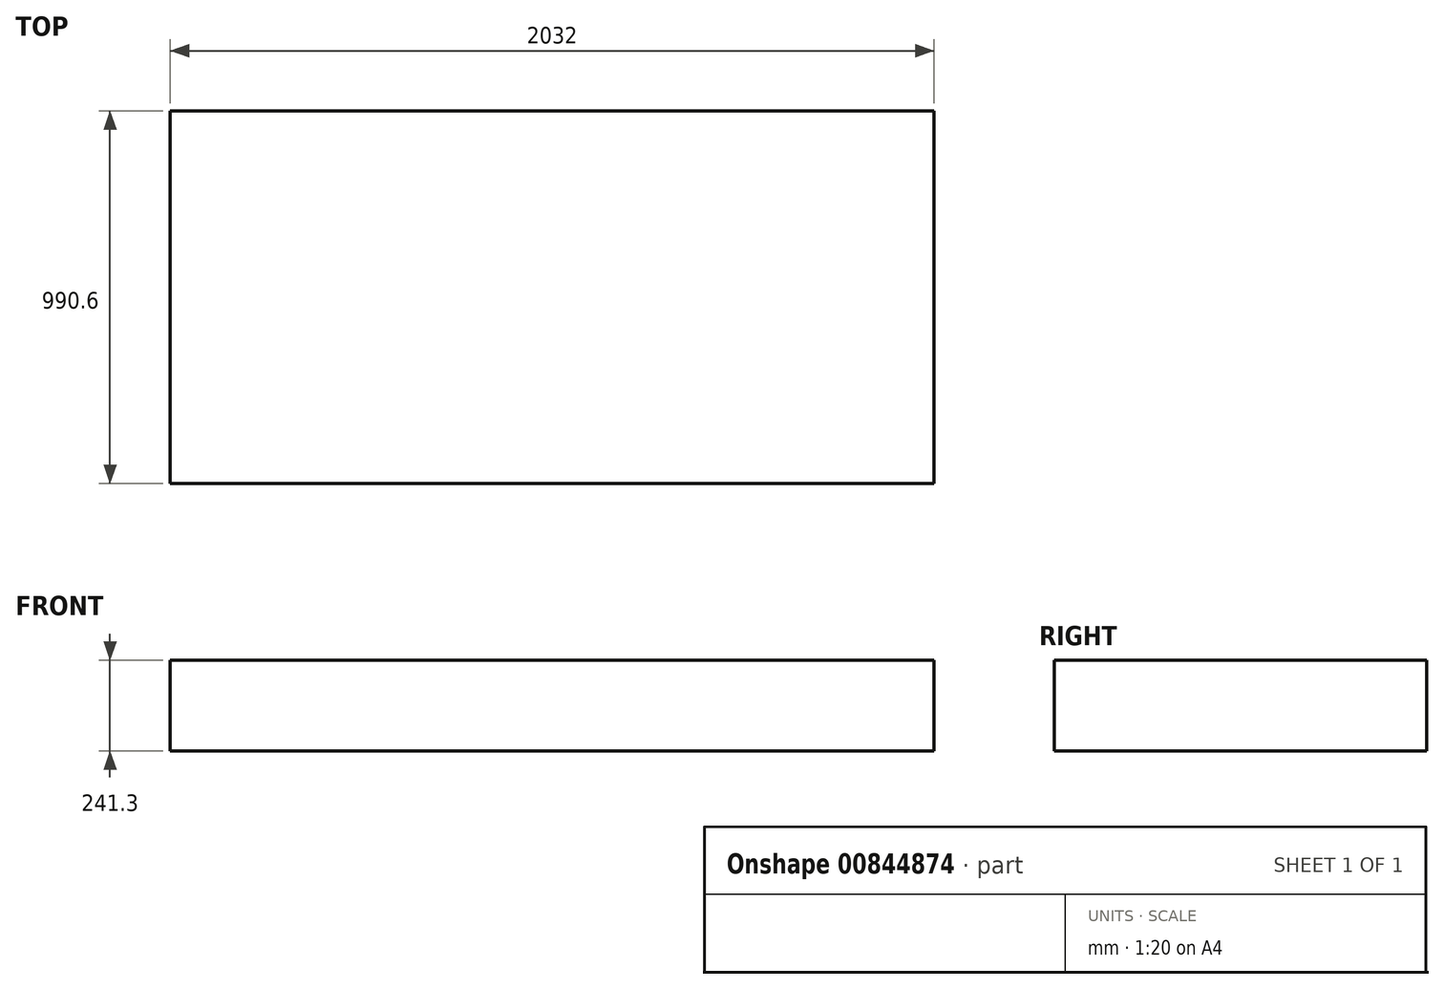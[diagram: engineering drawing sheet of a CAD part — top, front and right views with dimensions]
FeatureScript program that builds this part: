
annotation { "Feature Type Name" : "Feature", "Feature Type Description" : "" }
export const myFeature = defineFeature(function(context is Context, id is Id, definition is map)
    precondition{}
    {
        {
            var Q0;
            Q0=qCreatedBy(makeId("Top.planeOp"),FACE);
            var sketch = newSketch(context, id + "F0", { "sketchPlane" : qUnion([Q0])});
            skLineSegment(sketch, "E0.bottom", {"start": v(0, 0) * mm, "end": v(-2032, 0) * mm});
            skLineSegment(sketch, "E0.top", {"start": v(0, 990.6) * mm, "end": v(-2032, 990.6) * mm});
            skLineSegment(sketch, "E0.left", {"start": v(0, 0) * mm, "end": v(0, 990.6) * mm});
            skLineSegment(sketch, "E0.right", {"start": v(-2032, 0) * mm, "end": v(-2032, 990.6) * mm});
            skSolve(sketch);
        }
        {
            var Q0;
            Q0=makeQuery(id+"F0.imprint","IMPRINT",FACE,{"disambiguationData":[TD([[makeQuery(id+"F0.imprint","IMPRINT",EDGE,{"derivedFrom":sQuery(id+"F0.wireOp",EDGE,"E0.bottom")}),-1.0]])]});
            extrude(context, id + "F1", {"entities" : qUnion([Q0]), "depth" : 241.3 * mm, "offsetDistance" : 25.4 * mm});
        }
    });
